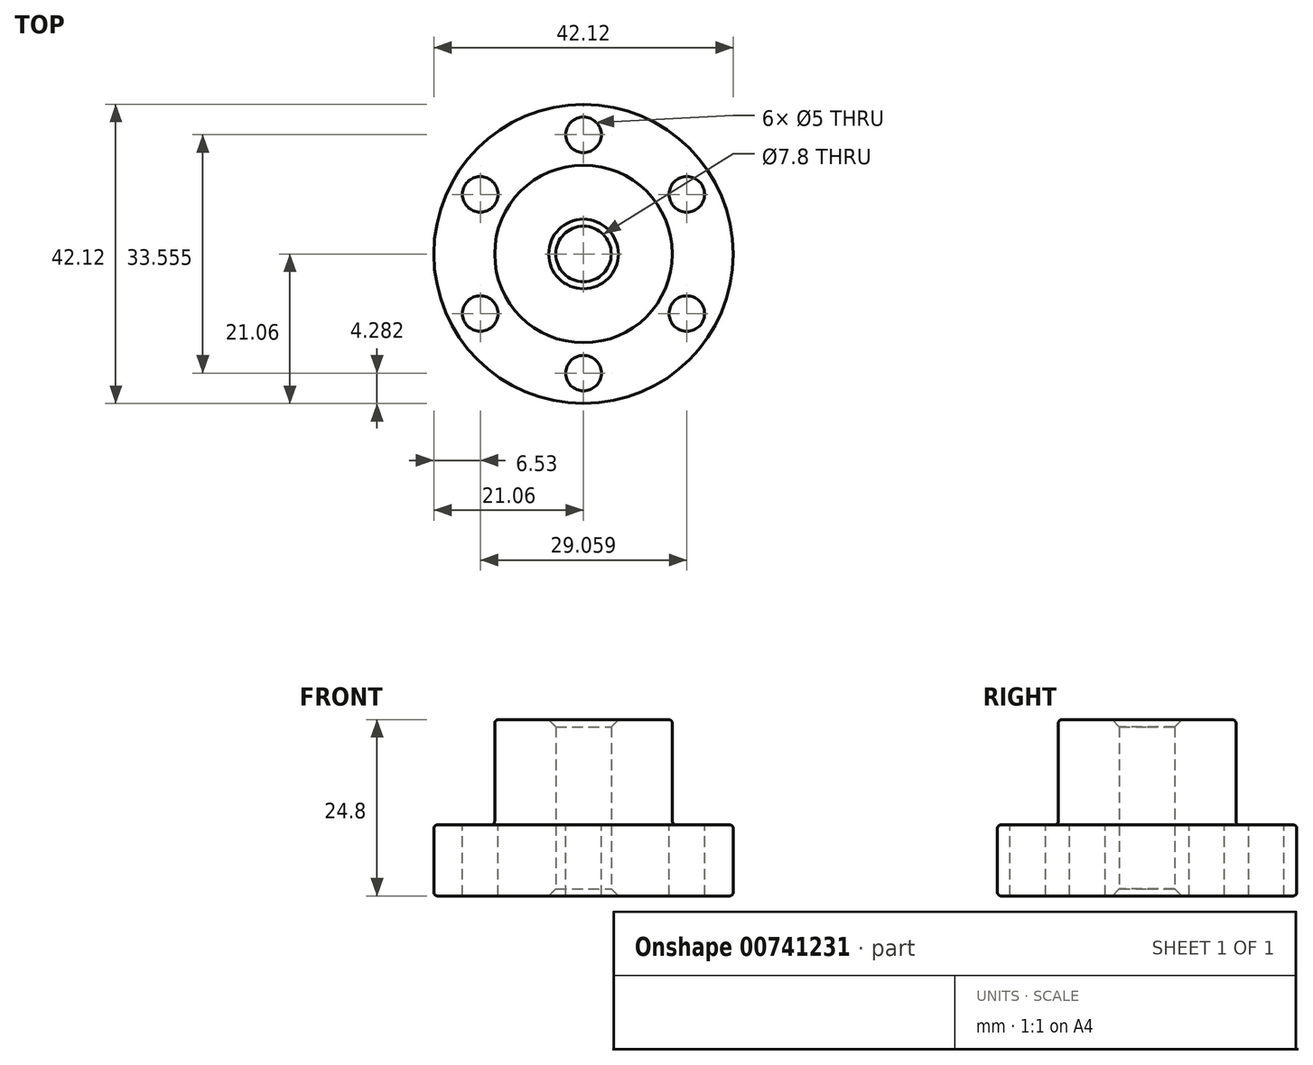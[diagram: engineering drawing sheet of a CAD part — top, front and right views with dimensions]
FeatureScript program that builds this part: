
annotation { "Feature Type Name" : "Feature", "Feature Type Description" : "" }
export const myFeature = defineFeature(function(context is Context, id is Id, definition is map)
    precondition{}
    {
        {
            var Q0;
            Q0=qCreatedBy(makeId("Front.planeOp"),FACE);
            var sketch = newSketch(context, id + "F0", { "sketchPlane" : qUnion([Q0])});
            skLineSegment(sketch, "E0", {"start": v(-21.05, 0) * mm, "end": v(-21.05, 10) * mm});
            skLineSegment(sketch, "E1", {"start": v(-21.05, 10) * mm, "end": v(-12.5, 10) * mm});
            skLineSegment(sketch, "E2", {"start": v(-12.5, 10) * mm, "end": v(-12.5, 24.8) * mm});
            skLineSegment(sketch, "E3", {"start": v(0, 24.8) * mm, "end": v(0, 0) * mm});
            skLineSegment(sketch, "E4", {"start": v(0, -26.76) * mm, "end": v(0, 64.94) * mm, "construction": true});
            skLineSegment(sketch, "E5", {"start": v(-3.9, 24.8) * mm, "end": v(-3.9, 0) * mm});
            skLineSegment(sketch, "E6", {"start": v(-3.9, 0) * mm, "end": v(-21.05, 0) * mm});
            skLineSegment(sketch, "E7", {"start": v(-3.9, 24.8) * mm, "end": v(-12.5, 24.8) * mm});
            skSolve(sketch);
        }
        {
            var Q0;
            Q0=makeQuery(id+"F0.imprint","IMPRINT",FACE,{"disambiguationData":[TD([[makeQuery(id+"F0.imprint","IMPRINT",EDGE,{"derivedFrom":sQuery(id+"F0.wireOp",EDGE,"E0")}),-1.0]])]});
            var Q1;
            Q1=sQuery(id+"F0.wireOp",EDGE,"E4");
            revolve(context, id + "F1", {"surfaceOperationType" : NewSurfaceOperationType.NEW, "entities" : qUnion([Q0]), "axis" : qUnion([Q1]), "revolveType" : RevolveType.FULL});
        }
        {
            var Q0;
            Q0=makeQuery(id+"F1.opRevolve","SWEPT_FACE",FACE,{"disambiguationData":[OSD([sQuery(id+"F0.wireOp",EDGE,"E1")])]});
            var sketch = newSketch(context, id + "F2", { "sketchPlane" : qUnion([Q0])});
            skLineSegment(sketch, "E8", {"start": v(0, 12.5) * mm, "end": v(0, 21.05) * mm, "construction": true});
            skCircle(sketch, "E9", {"center": v(0, 16.78) * mm, "radius": 2.5 * mm});
            skCircle(sketch, "E10.1.0", {"center": v(-14.53, 8.39) * mm, "radius": 2.5 * mm});
            skCircle(sketch, "E10.2.0", {"center": v(-14.53, -8.39) * mm, "radius": 2.5 * mm});
            skCircle(sketch, "E10.3.0", {"center": v(0, -16.78) * mm, "radius": 2.5 * mm});
            skCircle(sketch, "E10.4.0", {"center": v(14.53, -8.39) * mm, "radius": 2.5 * mm});
            skCircle(sketch, "E10.5.0", {"center": v(14.53, 8.39) * mm, "radius": 2.5 * mm});
            skPoint(sketch, "E10.center", {"position": v(0, 0) * mm});
            skSolve(sketch);
        }
        {
            var Q0;
            Q0 = qSketchRegion(id + "F2", true);
            extrude(context, id + "F3", {"entities" : qUnion([Q0]), "operationType" : NewBodyOperationType.REMOVE, "oppositeDirection" : true, "depth" : 25 * mm, "offsetDistance" : 25 * mm});
        }
        {
            var Q0;
            Q0=makeQuery(id+"F1.opRevolve","SWEPT_EDGE",EDGE,{"disambiguationData":[OSD([sQuery(id+"F0.wireOp",EDGE,"E2"),sQuery(id+"F0.wireOp",EDGE,"E7")])]});
            var Q1;
            Q1=makeQuery(id+"F1.opRevolve","SWEPT_EDGE",EDGE,{"disambiguationData":[OSD([sQuery(id+"F0.wireOp",EDGE,"E0"),sQuery(id+"F0.wireOp",EDGE,"E1")])]});
            var Q2;
            Q2=makeQuery(id+"F1.opRevolve","SWEPT_EDGE",EDGE,{"disambiguationData":[OSD([sQuery(id+"F0.wireOp",EDGE,"E0"),sQuery(id+"F0.wireOp",EDGE,"E6")])]});
            var Q3;
            Q3=makeQuery(id+"F1.opRevolve","SWEPT_EDGE",EDGE,{"disambiguationData":[OSD([sQuery(id+"F0.wireOp",EDGE,"E1"),sQuery(id+"F0.wireOp",EDGE,"E2")])]});
            fillet(context, id + "F4", {"entities" : qUnion([Q0, Q1, Q2, Q3]), "radius" : 0.5 * mm, "tangentPropagation" : true, "allowEdgeOverflow" : false});
        }
        {
            var Q0;
            Q0=makeQuery(id+"F1.opRevolve","SWEPT_EDGE",EDGE,{"disambiguationData":[OSD([sQuery(id+"F0.wireOp",EDGE,"E5"),sQuery(id+"F0.wireOp",EDGE,"E7")])]});
            var Q1;
            Q1=makeQuery(id+"F1.opRevolve","SWEPT_EDGE",EDGE,{"disambiguationData":[OSD([sQuery(id+"F0.wireOp",EDGE,"E5"),sQuery(id+"F0.wireOp",EDGE,"E6")])]});
            chamfer(context, id + "F5", {"entities" : qUnion([Q0, Q1]), "width" : 1 * mm, "tangentPropagation" : true});
        }
    });
